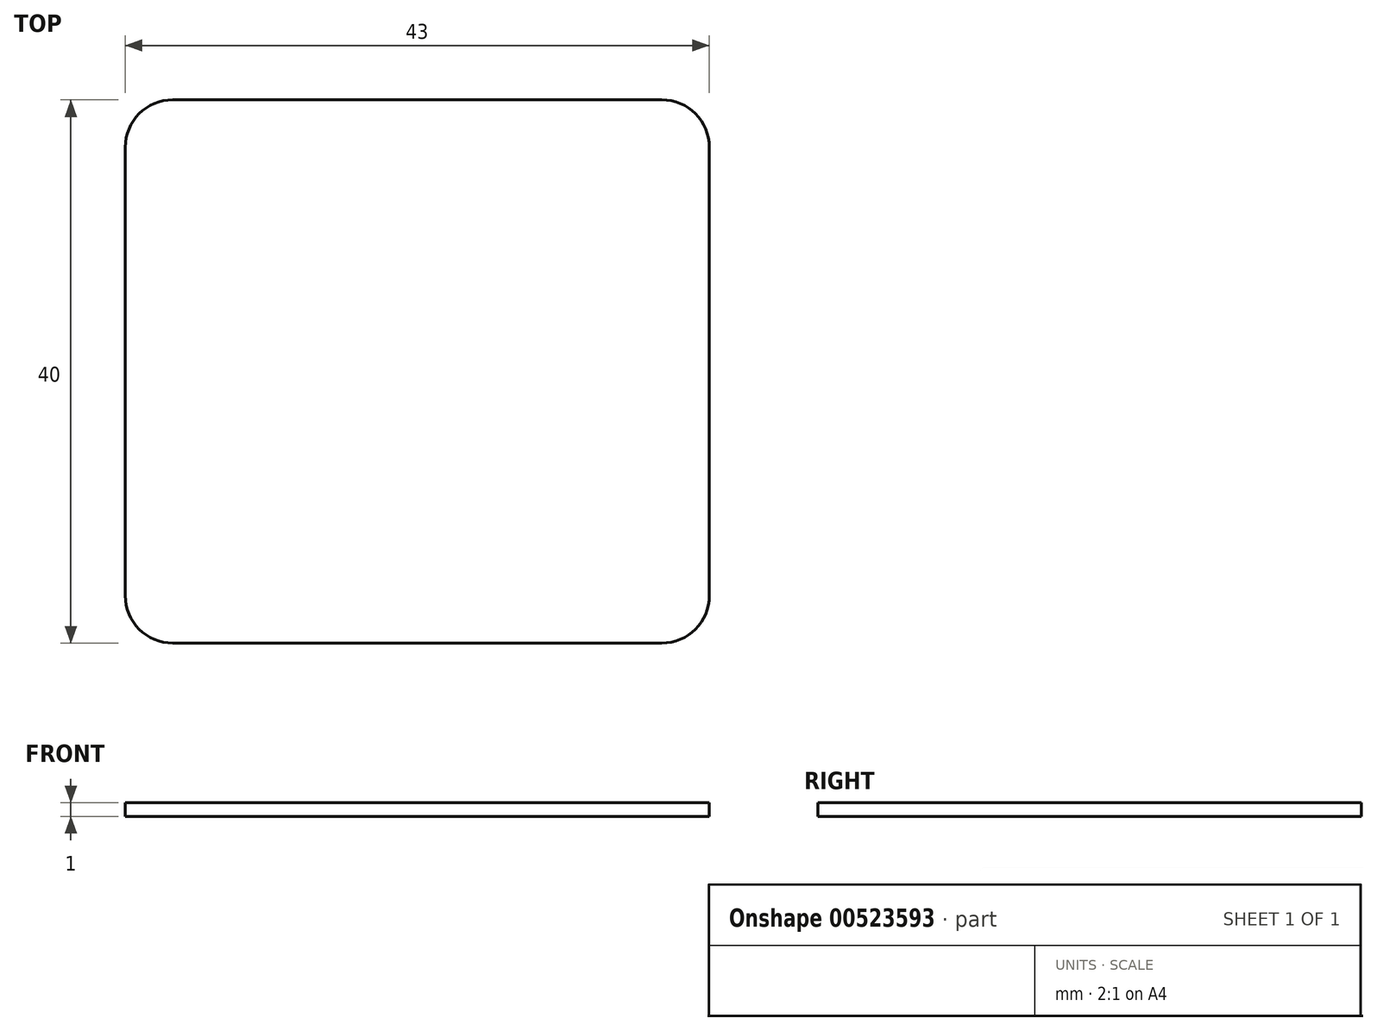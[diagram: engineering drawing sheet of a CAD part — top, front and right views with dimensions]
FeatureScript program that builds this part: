
annotation { "Feature Type Name" : "Feature", "Feature Type Description" : "" }
export const myFeature = defineFeature(function(context is Context, id is Id, definition is map)
    precondition{}
    {
        {
            var Q0;
            Q0=qCreatedBy(makeId("Top.planeOp"),FACE);
            var sketch = newSketch(context, id + "F0", { "sketchPlane" : qUnion([Q0])});
            skLineSegment(sketch, "E0.bottom", {"start": v(18, -20) * mm, "end": v(-18, -20) * mm});
            skLineSegment(sketch, "E0.top", {"start": v(18, 20) * mm, "end": v(-18, 20) * mm});
            skLineSegment(sketch, "E0.left", {"start": v(21.5, -16.5) * mm, "end": v(21.5, 16.5) * mm});
            skLineSegment(sketch, "E0.right", {"start": v(-21.5, -16.5) * mm, "end": v(-21.5, 16.5) * mm});
            skPoint(sketch, "E0.middle", {"position": v(0, 0) * mm});
            skPoint(sketch, "E1.visualSharp", {"position": v(-21.5, 20) * mm});
            skArc(sketch, "E1.filletArc", {"start": v(-18, 20) * mm, "mid": v(-20.47, 18.97) * mm, "end": v(-21.5, 16.5) * mm});
            skPoint(sketch, "E2.visualSharp", {"position": v(21.5, 20) * mm});
            skArc(sketch, "E2.filletArc", {"start": v(21.5, 16.5) * mm, "mid": v(20.47, 18.97) * mm, "end": v(18, 20) * mm});
            skPoint(sketch, "E3.visualSharp", {"position": v(-21.5, -20) * mm});
            skArc(sketch, "E3.filletArc", {"start": v(-21.5, -16.5) * mm, "mid": v(-20.47, -18.97) * mm, "end": v(-18, -20) * mm});
            skPoint(sketch, "E4.visualSharp", {"position": v(21.5, -20) * mm});
            skArc(sketch, "E4.filletArc", {"start": v(18, -20) * mm, "mid": v(20.47, -18.97) * mm, "end": v(21.5, -16.5) * mm});
            skSolve(sketch);
        }
        {
            var Q0;
            Q0=makeQuery(id+"F0.imprint","IMPRINT",FACE,{"disambiguationData":[TD([[makeQuery(id+"F0.imprint","IMPRINT",EDGE,{"derivedFrom":sQuery(id+"F0.wireOp",EDGE,"E0.bottom")}),-1.0]])]});
            extrude(context, id + "F1", {"entities" : qUnion([Q0]), "depth" : 1 * mm, "offsetDistance" : 25 * mm});
        }
    });
